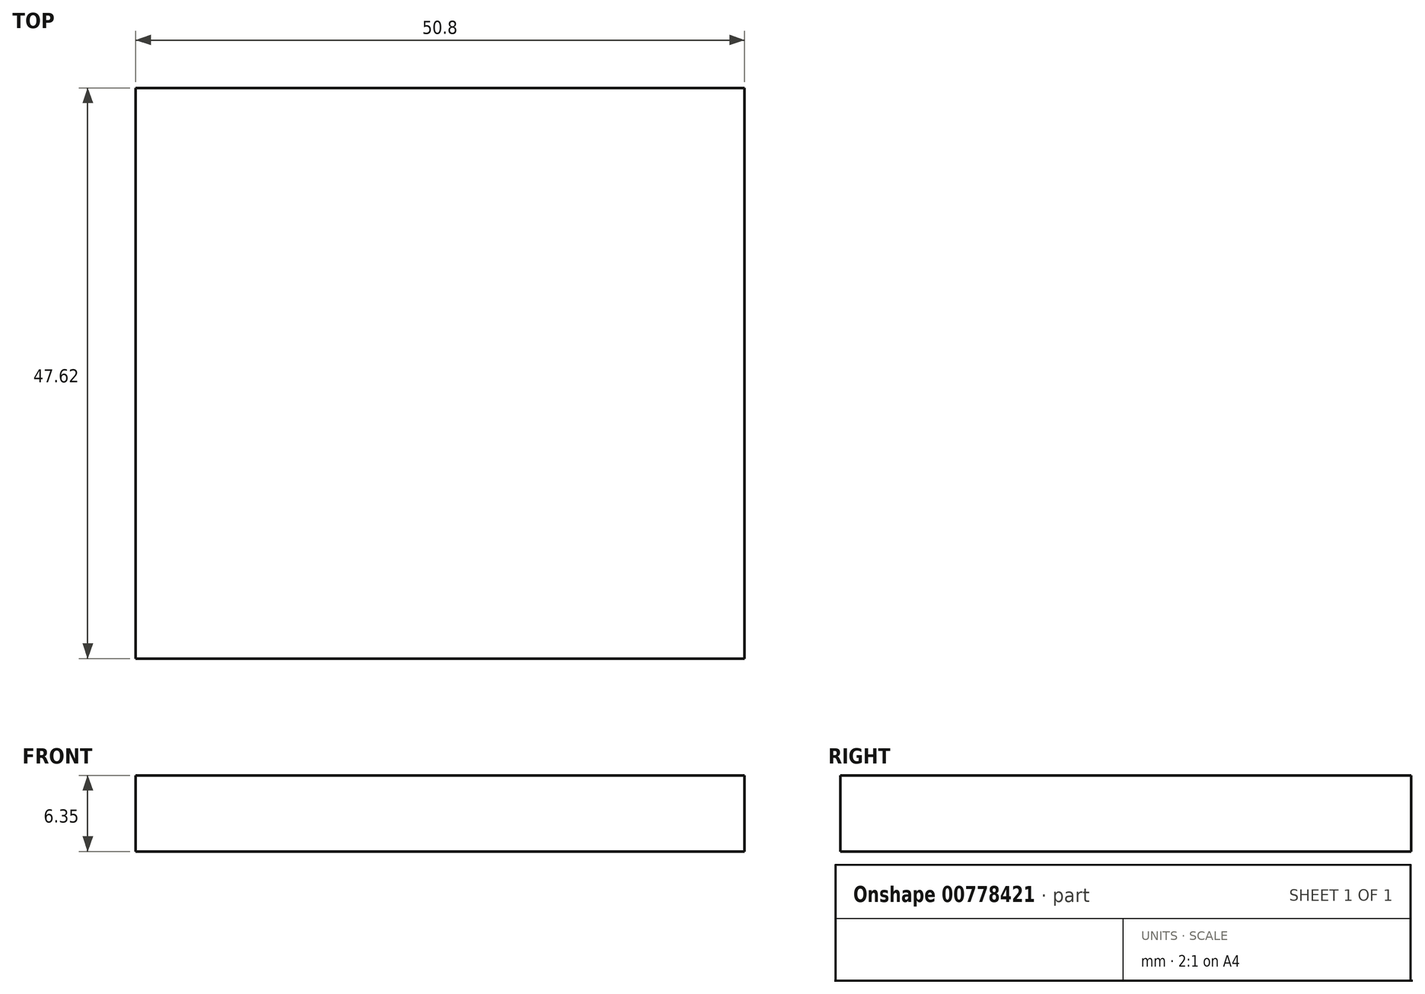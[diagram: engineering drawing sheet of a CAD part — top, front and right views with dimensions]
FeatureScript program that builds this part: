
annotation { "Feature Type Name" : "Feature", "Feature Type Description" : "" }
export const myFeature = defineFeature(function(context is Context, id is Id, definition is map)
    precondition{}
    {
        {
            var Q0;
            Q0=qCreatedBy(makeId("Top.planeOp"),FACE);
            var sketch = newSketch(context, id + "F0", { "sketchPlane" : qUnion([Q0])});
            skLineSegment(sketch, "E0.bottom", {"start": v(-25.4, -23.81) * mm, "end": v(25.4, -23.81) * mm});
            skLineSegment(sketch, "E0.top", {"start": v(-25.4, 23.81) * mm, "end": v(25.4, 23.81) * mm});
            skLineSegment(sketch, "E0.left", {"start": v(-25.4, -23.81) * mm, "end": v(-25.4, 23.81) * mm});
            skLineSegment(sketch, "E0.right", {"start": v(25.4, -23.81) * mm, "end": v(25.4, 23.81) * mm});
            skPoint(sketch, "E0.middle", {"position": v(0, 0) * mm});
            skSolve(sketch);
        }
        {
            var Q0;
            Q0=makeQuery(id+"F0.imprint","IMPRINT",FACE,{"disambiguationData":[TD([[makeQuery(id+"F0.imprint","IMPRINT",EDGE,{"derivedFrom":sQuery(id+"F0.wireOp",EDGE,"E0.bottom")}),1.0]])]});
            extrude(context, id + "F1", {"entities" : qUnion([Q0]), "depth" : 6.35 * mm, "offsetDistance" : 25.4 * mm});
        }
    });
